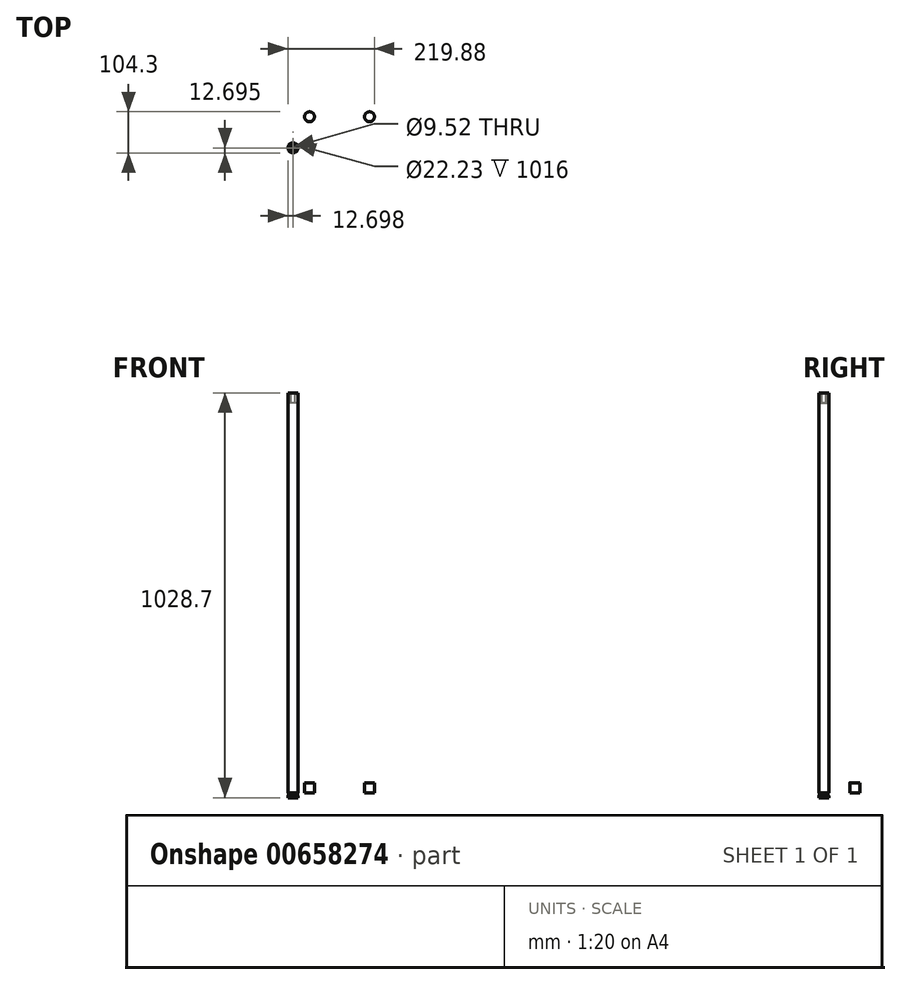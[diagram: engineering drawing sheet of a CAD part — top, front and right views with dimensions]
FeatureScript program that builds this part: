
annotation { "Feature Type Name" : "Feature", "Feature Type Description" : "" }
export const myFeature = defineFeature(function(context is Context, id is Id, definition is map)
    precondition{}
    {
        {
            var Q0;
            Q0=qCreatedBy(makeId("Top.planeOp"),FACE);
            var sketch = newSketch(context, id + "F0", { "sketchPlane" : qUnion([Q0])});
            skCircle(sketch, "E0", {"center": v(-52.6, -16.7) * mm, "radius": 12.7 * mm});
            skCircle(sketch, "E1", {"center": v(-52.6, -16.7) * mm, "radius": 11.11 * mm});
            skSolve(sketch);
        }
        {
            var Q0;
            Q0 = qSketchRegion(id + "F0", true);
            extrude(context, id + "F1", {"entities" : qUnion([Q0]), "depth" : 1016 * mm, "offsetDistance" : 25.4 * mm});
        }
        {
            var Q0;
            Q0=makeQuery(id+"F0.imprint","IMPRINT",FACE,{"disambiguationData":[TD([[makeQuery(id+"F0.imprint","IMPRINT",EDGE,{"derivedFrom":sQuery(id+"F0.wireOp",EDGE,"E1")}),1.0]])]});
            extrude(context, id + "F2", {"entities" : qUnion([Q0]), "operationType" : NewBodyOperationType.ADD, "oppositeDirection" : true, "depth" : 6.35 * mm, "offsetDistance" : 25.4 * mm});
        }
        {
            var Q0;
            Q0=makeQuery(id+"F2.opExtrude","CAP_FACE",FACE,{"disambiguationData":[OSD([sQuery(id+"F0.wireOp",EDGE,"E1")])],"isStart":false});
            var sketch = newSketch(context, id + "F3", { "sketchPlane" : qUnion([Q0])});
            skCircle(sketch, "E2", {"center": v(-52.6, 16.7) * mm, "radius": 12.7 * mm});
            skSolve(sketch);
        }
        {
            var Q0;
            Q0 = qSketchRegion(id + "F3", true);
            extrude(context, id + "F4", {"entities" : qUnion([Q0]), "operationType" : NewBodyOperationType.ADD, "depth" : 6.35 * mm, "offsetDistance" : 25.4 * mm});
        }
        {
            var Q0;
            Q0=makeQuery(id+"F4.opExtrude","CAP_EDGE",EDGE,{"disambiguationData":[OSD([sQuery(id+"F3.wireOp",EDGE,"E2")])],"isStart":true});
            fillet(context, id + "F5", {"entities" : qUnion([Q0]), "radius" : 5.08 * mm, "tangentPropagation" : true, "allowEdgeOverflow" : false});
        }
        {
            var Q0;
            Q0=makeQuery(id+"F1.opExtrude","CAP_FACE",FACE,{"disambiguationData":[OSD([sQuery(id+"F0.wireOp",EDGE,"E0"),sQuery(id+"F0.wireOp",EDGE,"E1")])],"isStart":false});
            var sketch = newSketch(context, id + "F6", { "sketchPlane" : qUnion([Q0])});
            skCircle(sketch, "E3", {"center": v(-52.6, -16.7) * mm, "radius": 11.11 * mm});
            skCircle(sketch, "E4.0", {"center": v(-52.6, -16.7) * mm, "radius": 4.76 * mm});
            skSolve(sketch);
        }
        {
            var Q0;
            Q0 = qSketchRegion(id + "F6", true);
            extrude(context, id + "F7", {"entities" : qUnion([Q0]), "oppositeDirection" : true, "depth" : 25.4 * mm, "offsetDistance" : 25.4 * mm});
        }
        {
            var Q0;
            Q0 = qSketchRegion(id + "F6", true);
            extrude(context, id + "F8", {"entities" : qUnion([Q0]), "operationType" : NewBodyOperationType.ADD, "oppositeDirection" : true, "depth" : 25.4 * mm, "offsetDistance" : 25.4 * mm});
        }
        {
            var Q0;
            Q0=makeQuery(id+"F7.opExtrude","CAP_EDGE",EDGE,{"disambiguationData":[OSD([sQuery(id+"F6.wireOp",EDGE,"E3")])],"isStart":true});
            chamfer(context, id + "F9", {"entities" : qUnion([Q0]), "width" : 1.27 * mm, "tangentPropagation" : true});
        }
        {
            var Q0;
            Q0=makeQuery(id+"F7.opExtrude","CAP_EDGE",EDGE,{"disambiguationData":[OSD([sQuery(id+"F6.wireOp",EDGE,"E4.0")])],"isStart":true});
            fillet(context, id + "F10", {"entities" : qUnion([Q0]), "radius" : 5.08 * mm, "tangentPropagation" : true, "allowEdgeOverflow" : false});
        }
        {
            var Q0;
            Q0=qCreatedBy(makeId("Top.planeOp"),FACE);
            var sketch = newSketch(context, id + "F11", { "sketchPlane" : qUnion([Q0])});
            skLineSegment(sketch, "E5.bottom", {"start": v(-10.51, 62.2) * mm, "end": v(141.89, 62.2) * mm});
            skLineSegment(sketch, "E5.top", {"start": v(-10.51, -14) * mm, "end": v(141.89, -14) * mm});
            skLineSegment(sketch, "E5.left", {"start": v(-10.51, 62.2) * mm, "end": v(-10.51, -14) * mm});
            skLineSegment(sketch, "E5.right", {"start": v(141.89, 62.2) * mm, "end": v(141.89, -14) * mm});
            skSolve(sketch);
        }
        {
            var Q0;
            Q0=qCreatedBy(makeId("Top.planeOp"),FACE);
            var sketch = newSketch(context, id + "F12", { "sketchPlane" : qUnion([Q0])});
            skCircle(sketch, "E6", {"center": v(-10.51, 62.2) * mm, "radius": 12.7 * mm});
            skCircle(sketch, "E7", {"center": v(141.89, 62.2) * mm, "radius": 12.7 * mm});
            skSolve(sketch);
        }
        {
            var Q0;
            Q0 = qSketchRegion(id + "F12", true);
            extrude(context, id + "F13", {"entities" : qUnion([Q0]), "depth" : 25.4 * mm, "offsetDistance" : 25.4 * mm});
        }
        {
            var Q0;
            Q0=makeQuery(id+"F1.opExtrude","SWEPT_BODY",BODY,{"disambiguationData":[OSD([sQuery(id+"F0.wireOp",EDGE,"E0"),sQuery(id+"F0.wireOp",EDGE,"E1")])]});
            transform(context, id + "F14", {"entities" : qUnion([Q0]), "transformType" : TransformType.TRANSLATION_3D, "dx" : 0 * mm, "dy" : 0 * mm, "dz" : 0 * mm, "makeCopy" : false});
        }
    });
